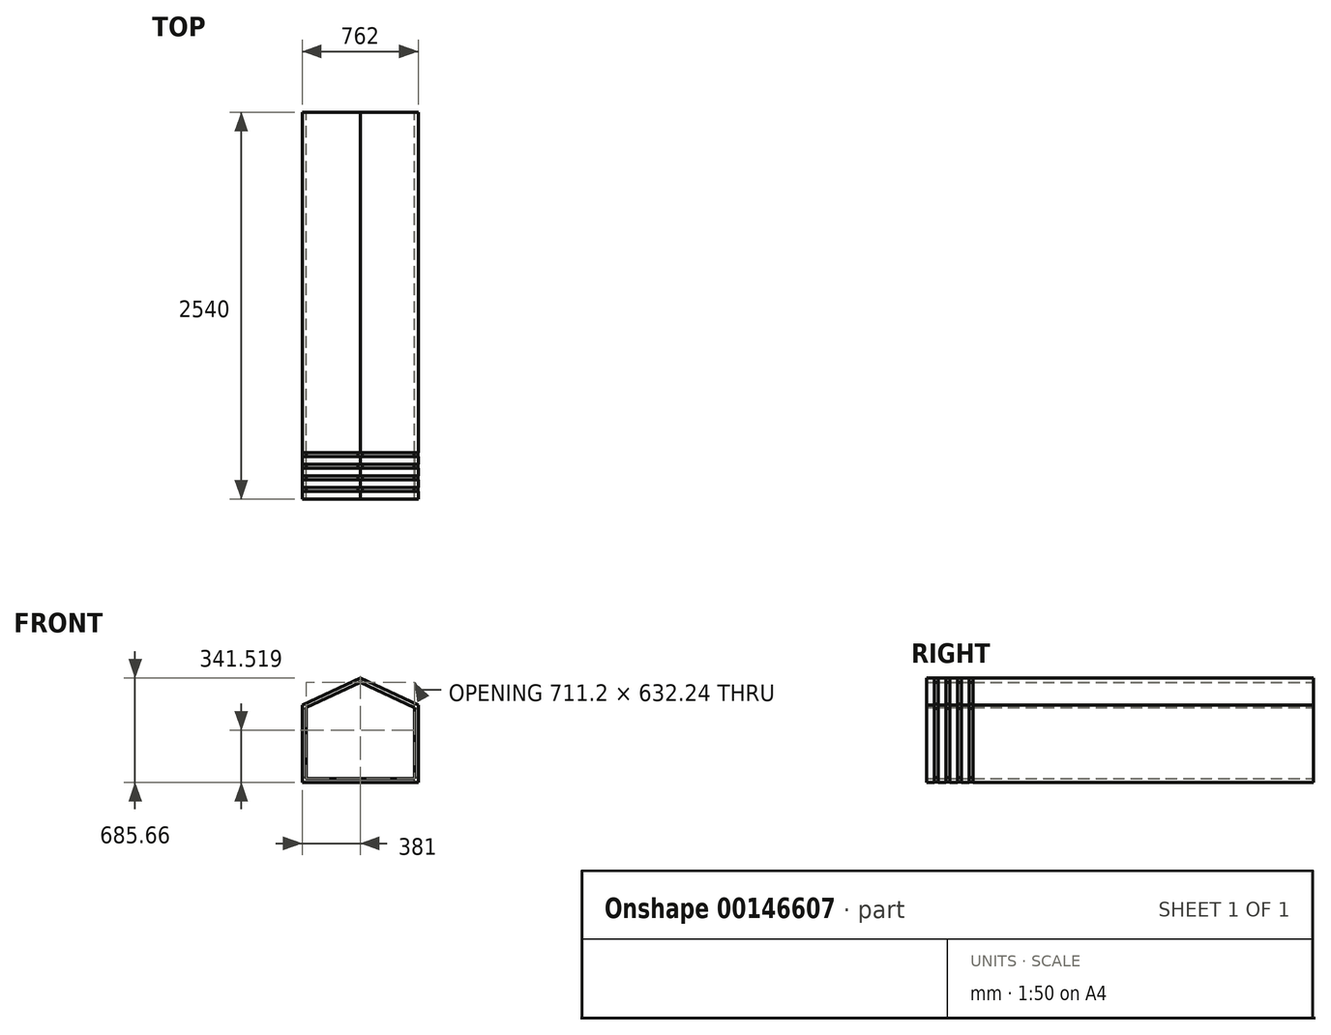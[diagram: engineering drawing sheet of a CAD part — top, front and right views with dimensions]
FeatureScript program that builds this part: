
annotation { "Feature Type Name" : "Feature", "Feature Type Description" : "" }
export const myFeature = defineFeature(function(context is Context, id is Id, definition is map)
    precondition{}
    {
        {
            var Q0;
            Q0=qCreatedBy(makeId("Front.planeOp"),FACE);
            var sketch = newSketch(context, id + "F0", { "sketchPlane" : qUnion([Q0])});
            skLineSegment(sketch, "E0", {"start": v(-381, 508) * mm, "end": v(-381, 0) * mm});
            skLineSegment(sketch, "E1", {"start": v(-381, 0) * mm, "end": v(381, 0) * mm});
            skLineSegment(sketch, "E2", {"start": v(381, 0) * mm, "end": v(381, 508) * mm});
            skLineSegment(sketch, "E3", {"start": v(381, 508) * mm, "end": v(0, 685.66) * mm});
            skLineSegment(sketch, "E4", {"start": v(0, 685.66) * mm, "end": v(-381, 508) * mm});
            skSolve(sketch);
        }
        {
            var Q0;
            Q0 = qSketchRegion(id + "F0", true);
            extrude(context, id + "F1", {"entities" : qUnion([Q0]), "depth" : 2540 * mm});
        }
        {
            var Q0;
            Q0=makeQuery(id+"F1.opExtrude","CAP_FACE",FACE,{"disambiguationData":[OSD([sQuery(id+"F0.wireOp",EDGE,"E0"),sQuery(id+"F0.wireOp",EDGE,"E1"),sQuery(id+"F0.wireOp",EDGE,"E2"),sQuery(id+"F0.wireOp",EDGE,"E3"),sQuery(id+"F0.wireOp",EDGE,"E4")])],"isStart":false});
            var Q1;
            Q1=makeQuery(id+"F1.opExtrude","CAP_FACE",FACE,{"disambiguationData":[OSD([sQuery(id+"F0.wireOp",EDGE,"E0"),sQuery(id+"F0.wireOp",EDGE,"E1"),sQuery(id+"F0.wireOp",EDGE,"E2"),sQuery(id+"F0.wireOp",EDGE,"E3"),sQuery(id+"F0.wireOp",EDGE,"E4")])],"isStart":true});
            shell(context, id + "F2", {"entities" : qUnion([Q0, Q1]), "thickness" : 25.4 * mm});
        }
        {
            var Q0;
            Q0=makeQuery(id+"F1.opExtrude","SWEPT_FACE",FACE,{"disambiguationData":[OSD([sQuery(id+"F0.wireOp",EDGE,"E1")])]});
            var sketch = newSketch(context, id + "F3", { "sketchPlane" : qUnion([Q0])});
            skLineSegment(sketch, "E5.bottom", {"start": v(-381, 2489.2) * mm, "end": v(381, 2489.2) * mm});
            skLineSegment(sketch, "E5.top", {"start": v(-381, 2463.8) * mm, "end": v(381, 2463.8) * mm});
            skLineSegment(sketch, "E5.left", {"start": v(-381, 2489.2) * mm, "end": v(-381, 2463.8) * mm});
            skLineSegment(sketch, "E5.right", {"start": v(381, 2489.2) * mm, "end": v(381, 2463.8) * mm});
            skLineSegment(sketch, "E6.0.1.0", {"start": v(-381, 2413) * mm, "end": v(381, 2413) * mm});
            skLineSegment(sketch, "E6.0.1.1", {"start": v(-381, 2387.6) * mm, "end": v(381, 2387.6) * mm});
            skLineSegment(sketch, "E6.0.1.2", {"start": v(-381, 2413) * mm, "end": v(-381, 2387.6) * mm});
            skLineSegment(sketch, "E6.0.1.3", {"start": v(381, 2413) * mm, "end": v(381, 2387.6) * mm});
            skLineSegment(sketch, "E6.0.2.0", {"start": v(-381, 2336.8) * mm, "end": v(381, 2336.8) * mm});
            skLineSegment(sketch, "E6.0.2.1", {"start": v(-381, 2311.4) * mm, "end": v(381, 2311.4) * mm});
            skLineSegment(sketch, "E6.0.2.2", {"start": v(-381, 2336.8) * mm, "end": v(-381, 2311.4) * mm});
            skLineSegment(sketch, "E6.0.2.3", {"start": v(381, 2336.8) * mm, "end": v(381, 2311.4) * mm});
            skLineSegment(sketch, "E6.0.3.0", {"start": v(-381, 2260.6) * mm, "end": v(381, 2260.6) * mm});
            skLineSegment(sketch, "E6.0.3.1", {"start": v(-381, 2235.2) * mm, "end": v(381, 2235.2) * mm});
            skLineSegment(sketch, "E6.0.3.2", {"start": v(-381, 2260.6) * mm, "end": v(-381, 2235.2) * mm});
            skLineSegment(sketch, "E6.0.3.3", {"start": v(381, 2260.6) * mm, "end": v(381, 2235.2) * mm});
            skLineSegment(sketch, "E6.direction1", {"start": v(-381, 2489.2) * mm, "end": v(-355.6, 2489.2) * mm, "construction": true});
            skLineSegment(sketch, "E6.direction2", {"start": v(-381, 2489.2) * mm, "end": v(-381, 2413) * mm, "construction": true});
            skSolve(sketch);
        }
        {
            var Q0;
            Q0=makeQuery(id+"F3.imprint","IMPRINT",FACE,{"disambiguationData":[TD([[makeQuery(id+"F3.imprint","IMPRINT",EDGE,{"derivedFrom":sQuery(id+"F3.wireOp",EDGE,"E5.bottom")}),-1.0]])]});
            var Q1;
            Q1=makeQuery(id+"F3.imprint","IMPRINT",FACE,{"disambiguationData":[TD([[makeQuery(id+"F3.imprint","IMPRINT",EDGE,{"derivedFrom":sQuery(id+"F3.wireOp",EDGE,"E6.0.1.0")}),-1.0]])]});
            var Q2;
            Q2=makeQuery(id+"F3.imprint","IMPRINT",FACE,{"disambiguationData":[TD([[makeQuery(id+"F3.imprint","IMPRINT",EDGE,{"derivedFrom":sQuery(id+"F3.wireOp",EDGE,"E6.0.2.0")}),-1.0]])]});
            var Q3;
            Q3=makeQuery(id+"F3.imprint","IMPRINT",FACE,{"disambiguationData":[TD([[makeQuery(id+"F3.imprint","IMPRINT",EDGE,{"derivedFrom":sQuery(id+"F3.wireOp",EDGE,"E6.0.3.0")}),-1.0]])]});
            extrude(context, id + "F4", {"entities" : qUnion([Q0, Q1, Q2, Q3]), "operationType" : NewBodyOperationType.REMOVE, "endBound" : BoundingType.THROUGH_ALL, "oppositeDirection" : true, "depth" : 25.4 * mm});
        }
        {
            var Q0;
            Q0=makeQuery(id+"F1.opExtrude","CAP_FACE",FACE,{"disambiguationData":[OSD([sQuery(id+"F0.wireOp",EDGE,"E0"),sQuery(id+"F0.wireOp",EDGE,"E1"),sQuery(id+"F0.wireOp",EDGE,"E2"),sQuery(id+"F0.wireOp",EDGE,"E3"),sQuery(id+"F0.wireOp",EDGE,"E4")])],"isStart":false});
            var sketch = newSketch(context, id + "F5", { "sketchPlane" : qUnion([Q0])});
            skCircle(sketch, "E7", {"center": v(0, 670.96) * mm, "radius": 13.32 * mm});
            skCircle(sketch, "E8", {"center": v(-367.22, 499.22) * mm, "radius": 13.78 * mm});
            skCircle(sketch, "E9.0.1.0", {"center": v(-367.22, 16.62) * mm, "radius": 13.78 * mm});
            skCircle(sketch, "E9.1.0.0", {"center": v(366.84, 499.22) * mm, "radius": 13.78 * mm});
            skCircle(sketch, "E9.1.1.0", {"center": v(366.84, 16.62) * mm, "radius": 13.78 * mm});
            skLineSegment(sketch, "E9.direction1", {"start": v(-367.22, 499.22) * mm, "end": v(366.84, 499.22) * mm, "construction": true});
            skLineSegment(sketch, "E9.direction2", {"start": v(-367.22, 499.22) * mm, "end": v(-367.22, 16.62) * mm, "construction": true});
            skSolve(sketch);
        }
        {
            var Q0;
            Q0 = qSketchRegion(id + "F5", true);
            var Q1;
            Q1 = qConstructionFilter(qBodyType(qCreatedBy(id + "F5" ,EDGE), BodyType.WIRE), ConstructionObject.NO);
            var Q2;
            Q2=makeQuery(id+"F4.boolean.opBoolean","COPY",FACE,{"derivedFrom":makeQuery(id+"F4.opExtrude","SWEPT_FACE",FACE,{"disambiguationData":[OSD([sQuery(id+"F3.wireOp",EDGE,"E6.0.3.1")])]})});
            extrude(context, id + "F6", {"entities" : qUnion([Q0]), "operationType" : NewBodyOperationType.ADD, "surfaceEntities" : qUnion([Q1]), "endBound" : BoundingType.UP_TO_SURFACE, "oppositeDirection" : true, "endBoundEntityFace" : qUnion([Q2]), "depth" : 25.4 * mm});
        }
    });
